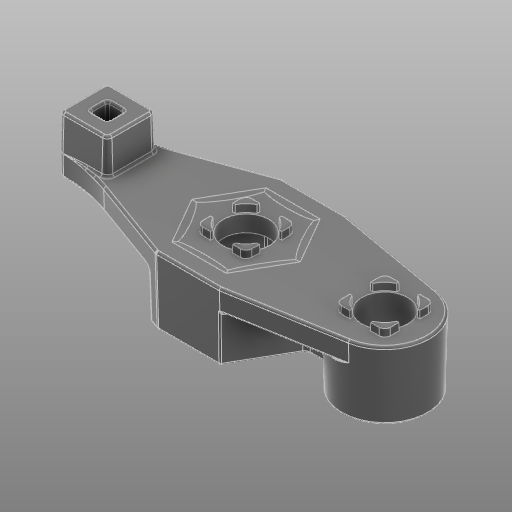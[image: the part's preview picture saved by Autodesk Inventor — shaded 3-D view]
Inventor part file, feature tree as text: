
AUTODESK INVENTOR PART (.ipt)
format: ipt  version: 2021 (Build 250183000, 183)  size: 753,152 bytes
history: native  units: in
note: dims shown in document units (in); Inventor stores cm internally (conversion verified against a paired STEP export)
features: fillet x1
ambient origin geometry x8: Origin, YZ Plane, XZ Plane, XY Plane, X Axis, Y Axis, Z Axis, Center Point
bodies: Solid1 (feature_tree)
feature tree (1):
  fillet  "Fillet15"  [1 undecoded]
note: 1 required parameter value undecoded (feature->parameter linkage not recoverable at this tier; creation-order binding heuristic only, values carry confidence <= 0.55)
